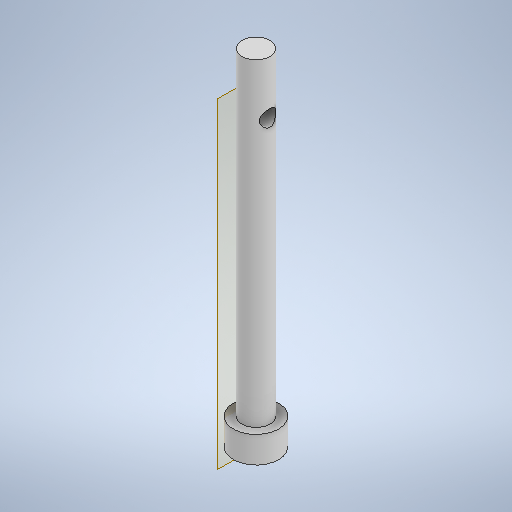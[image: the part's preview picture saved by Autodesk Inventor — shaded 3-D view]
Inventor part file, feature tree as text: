
AUTODESK INVENTOR PART (.ipt)
format: ipt  version: 2025.2 (Build 292293000, 293)  size: 252,416 bytes
history: native  units: mm
features: sketch x4, extrude x3, other x2
ambient origin geometry x8: Origin, YZ Plane, XZ Plane, XY Plane, X Axis, Y Axis, Z Axis, Center Point
bodies: Body1 (feature_tree)
feature tree (9):
  other  "Bryła1"
  extrude  "Wyciągnięcie proste1"  Depth=8.5mm
  extrude  "Wyciągnięcie proste2"  Depth=5.0mm TaperAngle=0.0deg
  other  "Płaszczyzna konstrukcyjna1"
  sketch  "Szkic3"
  extrude  "Wyciągnięcie proste3"  Depth=5.3mm
  sketch  "Szkic1"
  sketch  "Szkic2"
  sketch  "Szkic4"
